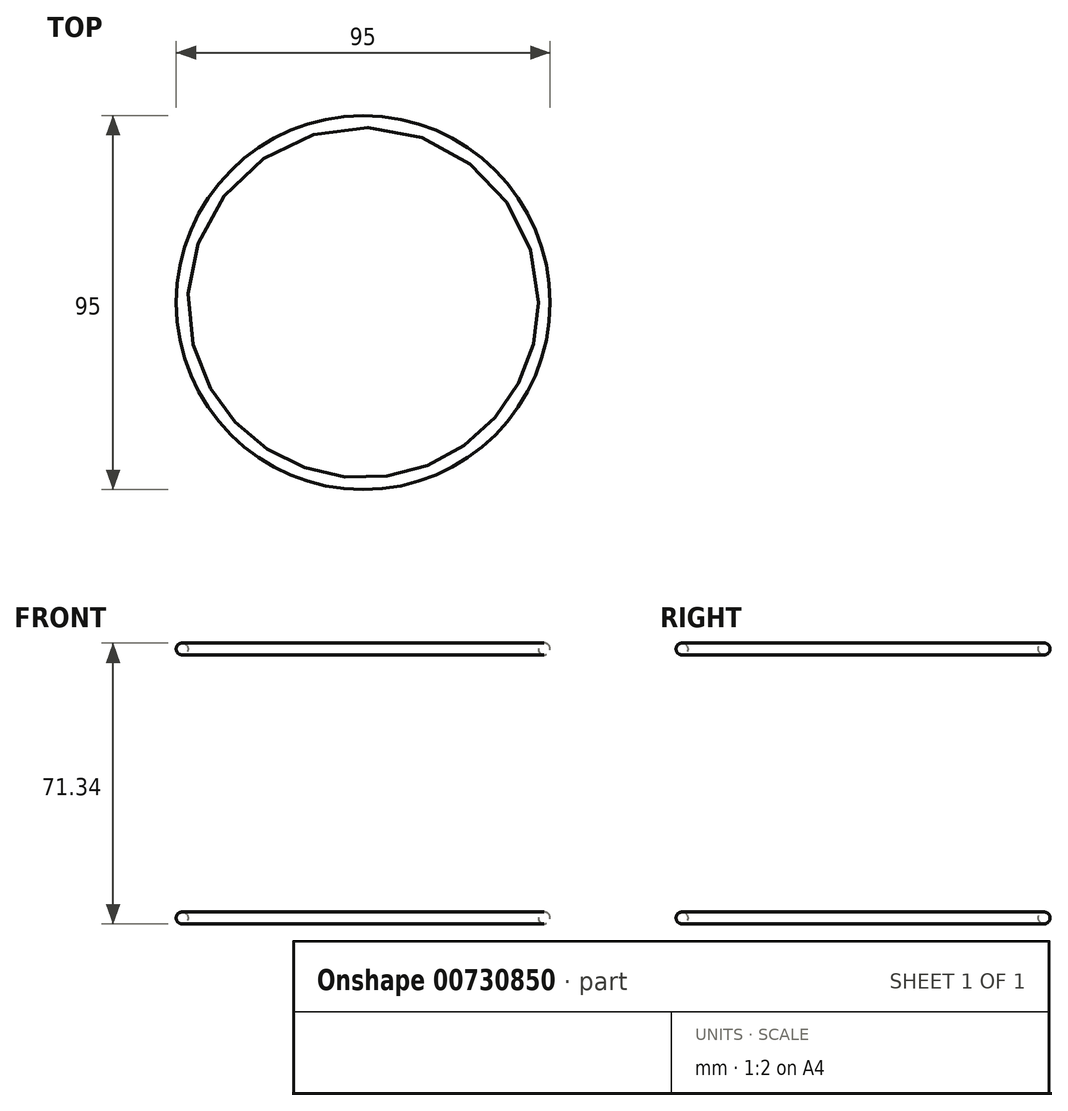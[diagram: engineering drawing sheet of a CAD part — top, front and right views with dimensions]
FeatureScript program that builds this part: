
annotation { "Feature Type Name" : "Feature", "Feature Type Description" : "" }
export const myFeature = defineFeature(function(context is Context, id is Id, definition is map)
    precondition{}
    {
        {
            var Q0;
            Q0=qCreatedBy(makeId("Front.planeOp"),FACE);
            var sketch = newSketch(context, id + "F0", { "sketchPlane" : qUnion([Q0])});
            skLineSegment(sketch, "E0", {"start": v(0, 55.44) * mm, "end": v(0, -54.55) * mm});
            skSolve(sketch);
        }
        {
            var Q0;
            Q0=qCreatedBy(makeId("Front.planeOp"),FACE);
            var sketch = newSketch(context, id + "F1", { "sketchPlane" : qUnion([Q0])});
            skCircle(sketch, "E1", {"center": v(46, 34.17) * mm, "radius": 1.5 * mm});
            skCircle(sketch, "E2", {"center": v(46, -34.17) * mm, "radius": 1.5 * mm});
            skPoint(sketch, "E3", {"position": v(-30.9, 34.17) * mm});
            skPoint(sketch, "E4", {"position": v(-30.9, -34.17) * mm});
            skSolve(sketch);
        }
        {
            var Q0;
            Q0=makeQuery(id+"F1.imprint","IMPRINT",FACE,{"disambiguationData":[TD([[makeQuery(id+"F1.imprint","IMPRINT",EDGE,{"derivedFrom":sQuery(id+"F1.wireOp",EDGE,"E2")}),1.0]])]});
            var Q1;
            Q1=makeQuery(id+"F1.imprint","IMPRINT",FACE,{"disambiguationData":[TD([[makeQuery(id+"F1.imprint","IMPRINT",EDGE,{"derivedFrom":sQuery(id+"F1.wireOp",EDGE,"E1")}),1.0]])]});
            var Q2;
            Q2=sQuery(id+"F0.wireOp",EDGE,"E0");
            revolve(context, id + "F2", {"surfaceOperationType" : NewSurfaceOperationType.NEW, "entities" : qUnion([Q0, Q1]), "axis" : qUnion([Q2]), "revolveType" : RevolveType.FULL});
        }
    });
